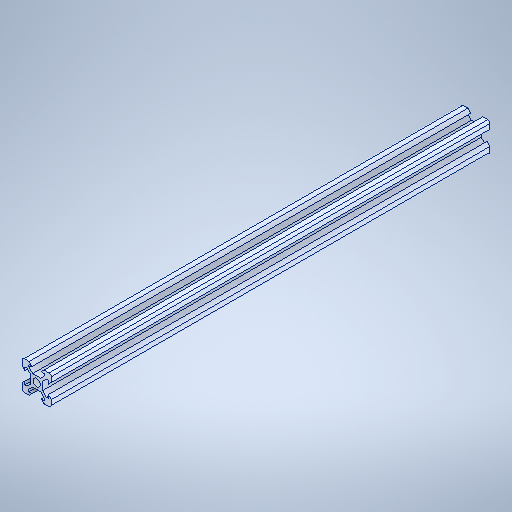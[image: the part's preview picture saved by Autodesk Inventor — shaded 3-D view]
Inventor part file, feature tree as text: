
AUTODESK INVENTOR PART (.ipt)
format: ipt  version: 2025.1 (Build 291241020, 241B)  size: 390,144 bytes
history: native  units: in
note: dims shown in document units (in); Inventor stores cm internally (conversion verified against a paired STEP export)
features: extrude x1, sketch x1, projected_geometry x1, other x1
ambient origin geometry x8: Origin, YZ Plane, XZ Plane, XY Plane, X Axis, Y Axis, Z Axis, Center Point
bodies: Solid1 (feature_tree)
feature tree (4):
  extrude  "Extrusion1"  Depth=11.811in
  sketch  "Sketch1"  dims[d0=11.811in d1=0.0in d2=0.0197in d3=0.0344in]
  projected_geometry  "Projected Loop1"
  other  "Скругление1"
